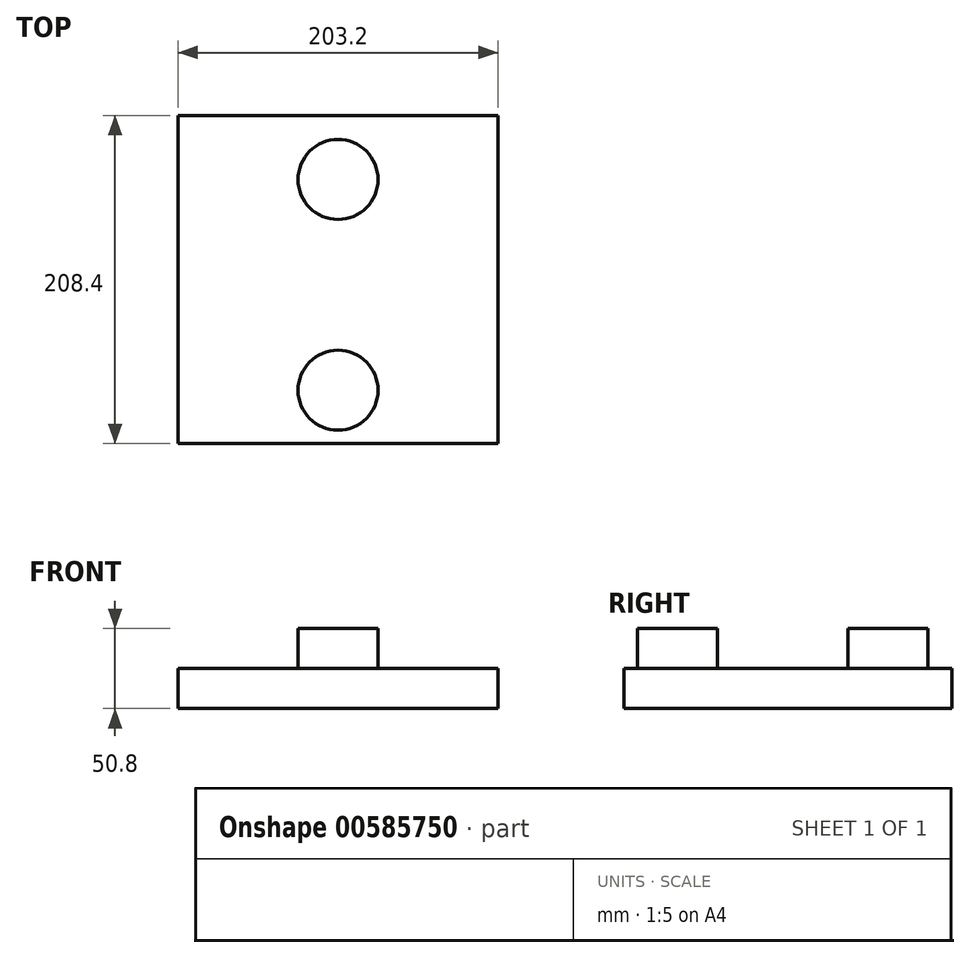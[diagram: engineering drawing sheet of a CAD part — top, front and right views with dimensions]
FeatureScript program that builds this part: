
annotation { "Feature Type Name" : "Feature", "Feature Type Description" : "" }
export const myFeature = defineFeature(function(context is Context, id is Id, definition is map)
    precondition{}
    {
        {
            var Q0;
            Q0=qCreatedBy(makeId("Top.planeOp"),FACE);
            var sketch = newSketch(context, id + "F0", { "sketchPlane" : qUnion([Q0])});
            skLineSegment(sketch, "E0.bottom", {"start": v(-101.6, 104.2) * mm, "end": v(101.6, 104.2) * mm});
            skLineSegment(sketch, "E0.top", {"start": v(-101.6, -104.2) * mm, "end": v(101.6, -104.2) * mm});
            skLineSegment(sketch, "E0.left", {"start": v(-101.6, 104.2) * mm, "end": v(-101.6, -104.2) * mm});
            skLineSegment(sketch, "E0.right", {"start": v(101.6, 104.2) * mm, "end": v(101.6, -104.2) * mm});
            skSolve(sketch);
        }
        {
            var Q0;
            Q0 = qSketchRegion(id + "F0", true);
            extrude(context, id + "F1", {"entities" : qUnion([Q0]), "depth" : 25.4 * mm, "offsetDistance" : 25.4 * mm});
        }
        {
            var Q0;
            Q0=makeQuery(id+"F1.opExtrude","CAP_FACE",FACE,{"disambiguationData":[OSD([sQuery(id+"F0.wireOp",EDGE,"E0.bottom"),sQuery(id+"F0.wireOp",EDGE,"E0.top"),sQuery(id+"F0.wireOp",EDGE,"E0.left"),sQuery(id+"F0.wireOp",EDGE,"E0.right")])],"isStart":false});
            var sketch = newSketch(context, id + "F2", { "sketchPlane" : qUnion([Q0])});
            skCircle(sketch, "E1", {"center": v(0, 63.5) * mm, "radius": 25.4 * mm});
            skSolve(sketch);
        }
        {
            var Q0;
            Q0 = qSketchRegion(id + "F2", true);
            extrude(context, id + "F3", {"entities" : qUnion([Q0]), "operationType" : NewBodyOperationType.ADD, "depth" : 25.4 * mm, "offsetDistance" : 25.4 * mm});
        }
        {
            var Q0;
            Q0=makeQuery(id+"F1.opExtrude","CAP_FACE",FACE,{"disambiguationData":[OSD([sQuery(id+"F0.wireOp",EDGE,"E0.bottom"),sQuery(id+"F0.wireOp",EDGE,"E0.top"),sQuery(id+"F0.wireOp",EDGE,"E0.left"),sQuery(id+"F0.wireOp",EDGE,"E0.right")])],"isStart":false});
            var sketch = newSketch(context, id + "F4", { "sketchPlane" : qUnion([Q0])});
            skCircle(sketch, "E2", {"center": v(0, -70.36) * mm, "radius": 25.4 * mm});
            skSolve(sketch);
        }
        {
            var Q0;
            Q0 = qSketchRegion(id + "F4", true);
            var Q1;
            Q1=makeQuery(id+"F3.opExtrude","CAP_FACE",FACE,{"disambiguationData":[OSD([sQuery(id+"F2.wireOp",EDGE,"E1")])],"isStart":false});
            extrude(context, id + "F5", {"entities" : qUnion([Q0]), "operationType" : NewBodyOperationType.ADD, "endBound" : BoundingType.UP_TO_SURFACE, "depth" : 25.4 * mm, "endBoundEntityFace" : qUnion([Q1]), "offsetDistance" : 25.4 * mm});
        }
    });
